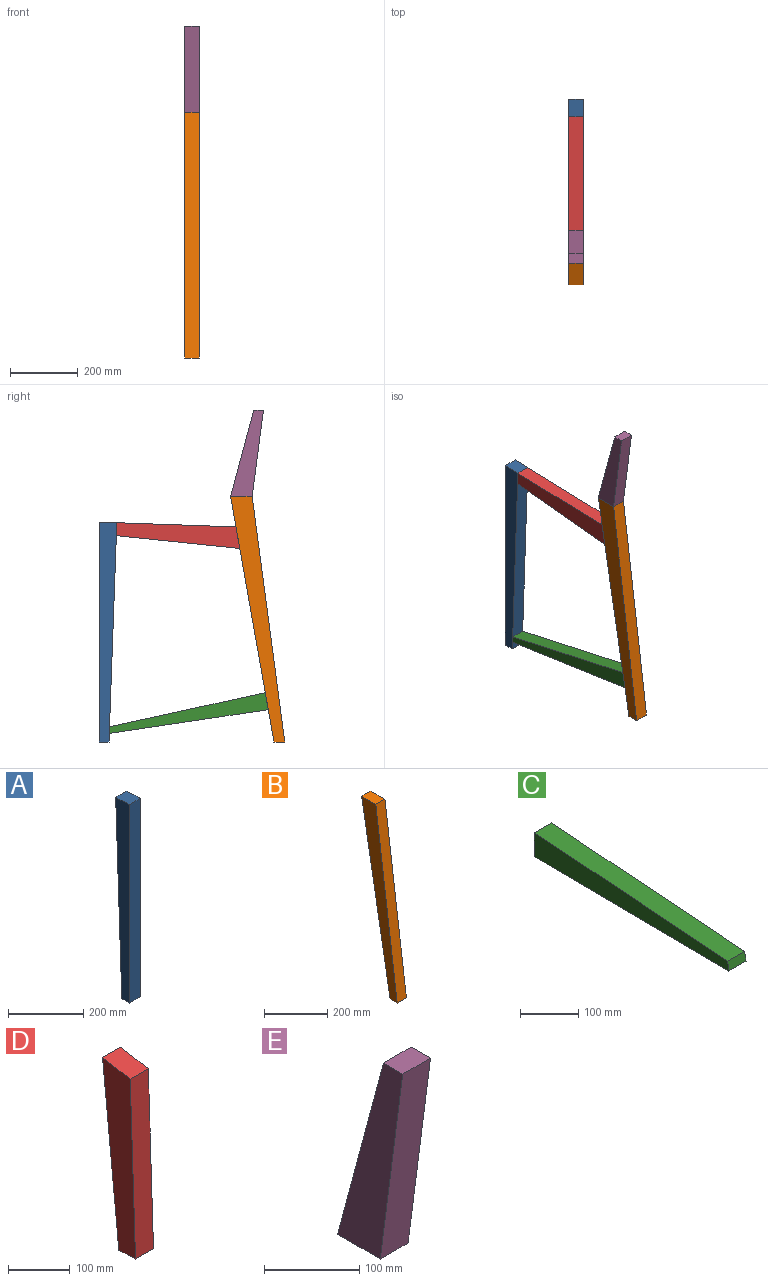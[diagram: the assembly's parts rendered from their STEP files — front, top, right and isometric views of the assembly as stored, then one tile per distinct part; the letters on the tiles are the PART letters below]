
ASSEMBLY  parts=5 mates=5
PART A: 6 faces, bbox 41.3x51.6x647.7 mm
  f0: plane 41.28x28.58mm, normal (0,0,-1), area 1179.4mm2, adj f1,f3,f4,f5
  f1: plane 645.9x41.28mm, normal (0,1,-0.04), area 26676.4mm2, adj f0,f2,f4,f5
  f2: plane 51.59x41.28mm, normal (0,0.03,1), area 2130.8mm2, adj f1,f3,f4,f5
  f3: plane 647.7x41.28mm, normal (0,-1,0), area 26733.8mm2, adj f0,f2,f4,f5
  f4: plane 647.7x51.59mm, normal (1,0,0), area 25936.9mm2, adj f0,f1,f2,f3
  f5: plane 647.7x51.59mm, normal (-1,0,0), area 25936.9mm2, adj f0,f1,f2,f3
PART B: 6 faces, bbox 41.3x159.4x723.9 mm
  f0: plane 723.9x95.89mm, normal (0,-0.99,0.13), area 30140mm2, adj f1,f3,f4,f5
  f1: plane 41.28x31.75mm, normal (0,0,-1), area 1310.5mm2, adj f0,f2,f4,f5
  f2: plane 723.9x127.64mm, normal (0,0.98,-0.17), area 30339.9mm2, adj f1,f3,f4,f5
  f3: plane 63.5x41.28mm, normal (0,0,1), area 2621mm2, adj f0,f2,f4,f5
  f4: plane 723.9x159.39mm, normal (1,0,0), area 34475.7mm2, adj f0,f1,f2,f3
  f5: plane 723.9x159.39mm, normal (-1,0,0), area 34475.7mm2, adj f0,f1,f2,f3
PART C: 6 faces, bbox 41.3x473.2x55 mm
  f0: plane 41.28x19.05mm, normal (0,-0.98,0.17), area 798.5mm2, adj f1,f3,f4,f5
  f1: plane 473.24x41.28mm, normal (0,0.01,-1), area 19533.8mm2, adj f0,f2,f4,f5
  f2: plane 50.8x41.28mm, normal (0,1,0.04), area 2098.1mm2, adj f1,f3,f4,f5
  f3: plane 468.09x41.28mm, normal (0,-0.08,1), area 19377.1mm2, adj f0,f2,f4,f5
  f4: plane 473.24x54.99mm, normal (1,0,0), area 16422.1mm2, adj f0,f1,f2,f3
  f5: plane 473.24x54.99mm, normal (-1,0,0), area 16422.1mm2, adj f0,f1,f2,f3
PART D: 6 faces, bbox 41.3x75.5x363.6 mm
  f0: plane 351.04x41.28mm, normal (0,-1,0.03), area 14497.5mm2, adj f1,f3,f4,f5
  f1: plane 41.28x38.1mm, normal (0,-0.03,-1), area 1573.5mm2, adj f0,f2,f4,f5
  f2: plane 363.61x41.28mm, normal (0,0.99,-0.1), area 15087.3mm2, adj f1,f3,f4,f5
  f3: plane 63.5x41.28mm, normal (0,-0.17,0.98), area 2661.7mm2, adj f0,f2,f4,f5
  f4: plane 363.61x75.51mm, normal (1,0,0), area 18029.6mm2, adj f0,f1,f2,f3
  f5: plane 363.61x75.51mm, normal (-1,0,0), area 18029.6mm2, adj f0,f1,f2,f3
PART E: 6 faces, bbox 41.3x96.6x254 mm
  f0: plane 254x41.28mm, normal (0,-0.99,-0.13), area 10572.7mm2, adj f1,f3,f4,f5
  f1: plane 63.5x41.28mm, normal (0,0,-1), area 2621mm2, adj f0,f2,f4,f5
  f2: plane 254x68.06mm, normal (0,0.97,0.26), area 10853.7mm2, adj f1,f3,f4,f5
  f3: plane 41.28x28.58mm, normal (0,0,1), area 1179.4mm2, adj f0,f2,f4,f5
  f4: plane 254x96.63mm, normal (1,0,0), area 11693.5mm2, adj f0,f1,f2,f3
  f5: plane 254x96.63mm, normal (-1,0,0), area 11693.5mm2, adj f0,f1,f2,f3
PLACE A rot(axis=(0,0,1),180deg) t=(-61.04,645.09,5.83)mm
PLACE B t=(-102.32,127.57,5.83)mm fixed
PLACE C rot(axis=(0,0.07,1),180deg) t=(-61.04,644.19,31.22)mm
PLACE D rot(axis=(0,-0.71,0.71),180deg) t=(-61.04,622.07,651.73)mm
PLACE E t=(-102.32,244.68,729.73)mm
MATE fastened D.f1 <-> A.f1  axis (0,1,0.04) through (-81.68,622.07,651.73)mm
MATE planar A.f0 <-> B.f1  axis (0,0,-1) through (-81.68,659.38,5.83)mm
MATE fastened B.f3 <-> E.f1  axis (0,0,1) through (-81.68,255.21,729.73)mm
MATE fastened B.f1 <-> A.f0  axis (0,0,-1) through (-81.68,159.32,5.83)mm
MATE fastened C.f0 <-> A.f1  axis (0,1,0.04) through (-81.68,644.19,31.22)mm
